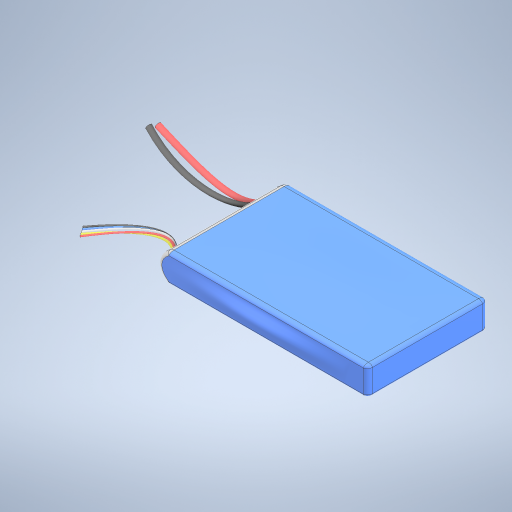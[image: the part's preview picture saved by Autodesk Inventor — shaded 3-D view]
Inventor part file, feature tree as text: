
AUTODESK INVENTOR PART (.ipt)
format: ipt  version: 2024.3 (Build 283343000, 343)  size: 635,392 bytes
history: native  units: in
note: dims shown in document units (in); Inventor stores cm internally (conversion verified against a paired STEP export)
features: other x4, plane x4, direct_edit x1, sweep x1
ambient origin geometry x8: Origin, YZ Plane, XZ Plane, XY Plane, X Axis, Y Axis, Z Axis, Center Point
bodies: Solid1 (feature_tree)
feature tree (10):
  other  "Plane1"
  other  "Plane2"
  direct_edit  "Direct Edit1"
  other  "Work Point1"
  plane  "Work Plane3"
  plane  "Work Plane4"
  plane  "Work Plane5"
  plane  "Work Plane6"
  sweep  "Sweep7"
  other  "Scale1"
